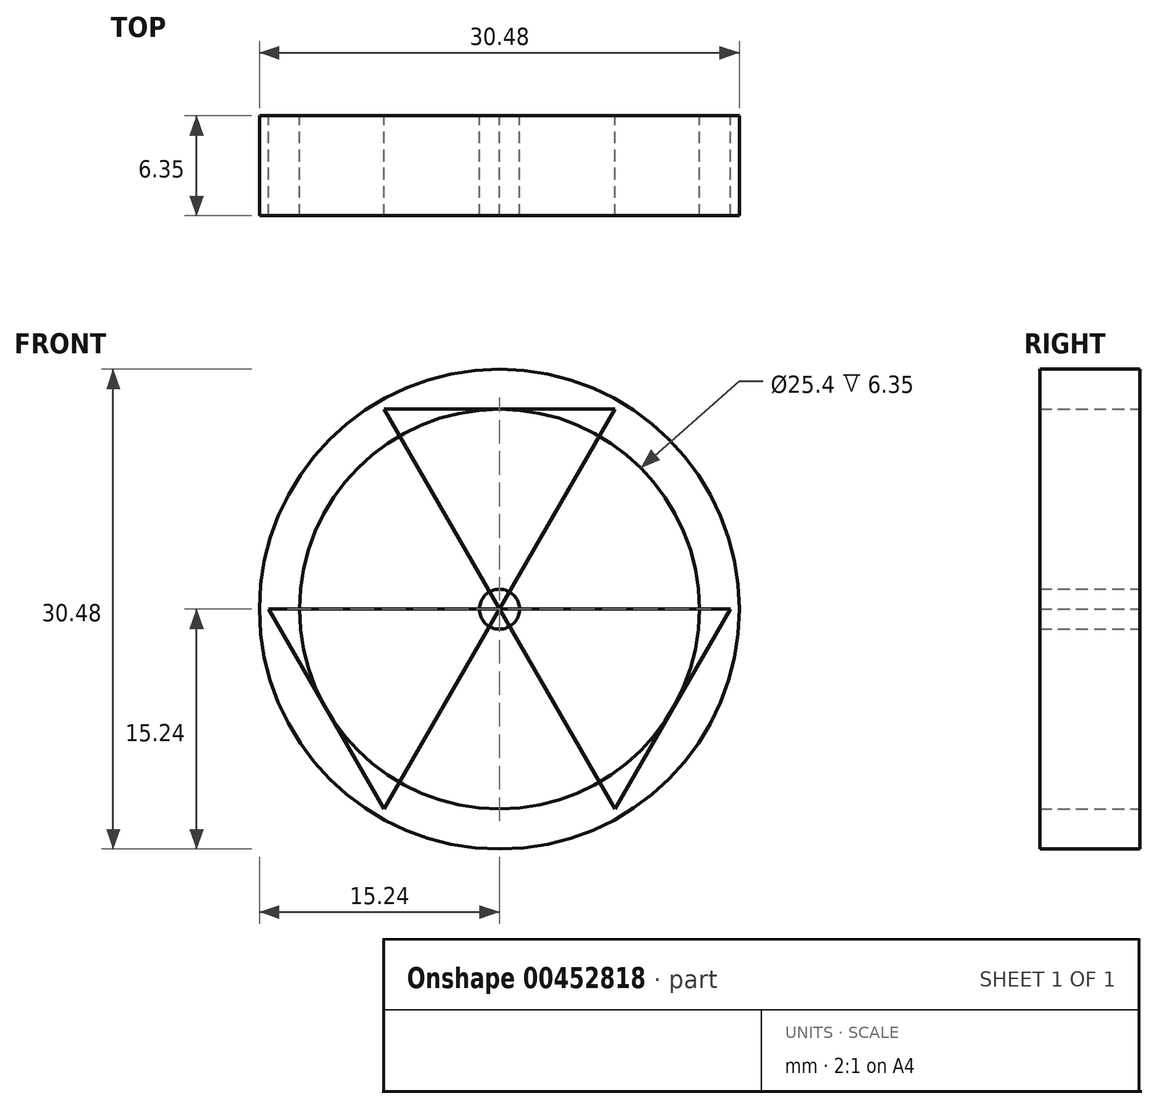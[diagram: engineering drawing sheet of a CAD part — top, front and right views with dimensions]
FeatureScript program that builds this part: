
annotation { "Feature Type Name" : "Feature", "Feature Type Description" : "" }
export const myFeature = defineFeature(function(context is Context, id is Id, definition is map)
    precondition{}
    {
        {
            var Q0;
            Q0=qCreatedBy(makeId("Front.planeOp"),FACE);
            var sketch = newSketch(context, id + "F0", { "sketchPlane" : qUnion([Q0])});
            skCircle(sketch, "E0.cCircle", {"center": v(0, 0) * mm, "radius": 12.7 * mm, "construction": true});
            skLineSegment(sketch, "E0.0", {"start": v(-7.33, 12.7) * mm, "end": v(7.33, 12.7) * mm});
            skLineSegment(sketch, "E0.1", {"start": v(7.33, 12.7) * mm, "end": v(14.66, 0) * mm});
            skLineSegment(sketch, "E0.2", {"start": v(14.66, 0) * mm, "end": v(7.33, -12.7) * mm});
            skLineSegment(sketch, "E0.3", {"start": v(7.33, -12.7) * mm, "end": v(-7.33, -12.7) * mm});
            skLineSegment(sketch, "E0.4", {"start": v(-7.33, -12.7) * mm, "end": v(-14.66, 0) * mm});
            skLineSegment(sketch, "E0.5", {"start": v(-14.66, 0) * mm, "end": v(-7.33, 12.7) * mm});
            skPoint(sketch, "E0.0.midPoint", {"position": v(0, 12.7) * mm});
            skLineSegment(sketch, "E1", {"start": v(-7.33, 12.7) * mm, "end": v(0, 0) * mm});
            skLineSegment(sketch, "E2", {"start": v(7.33, 12.7) * mm, "end": v(0, 0) * mm});
            skLineSegment(sketch, "E3", {"start": v(-14.66, 0) * mm, "end": v(0, 0) * mm});
            skLineSegment(sketch, "E4", {"start": v(-7.33, -12.7) * mm, "end": v(0, 0) * mm});
            skLineSegment(sketch, "E5", {"start": v(7.33, -12.7) * mm, "end": v(0, 0) * mm});
            skLineSegment(sketch, "E6", {"start": v(14.66, 0) * mm, "end": v(0, 0) * mm});
            skSolve(sketch);
        }
        {
            var Q0;
            Q0=makeQuery(id+"F0.imprint","IMPRINT",FACE,{"disambiguationData":[TD([[makeQuery(id+"F0.imprint","IMPRINT",EDGE,{"derivedFrom":sQuery(id+"F0.wireOp",EDGE,"E0.0")}),-1.0]])]});
            var Q1;
            Q1=makeQuery(id+"F0.imprint","IMPRINT",FACE,{"disambiguationData":[TD([[makeQuery(id+"F0.imprint","IMPRINT",EDGE,{"derivedFrom":sQuery(id+"F0.wireOp",EDGE,"E0.4")}),-1.0]])]});
            var Q2;
            Q2=makeQuery(id+"F0.imprint","IMPRINT",FACE,{"disambiguationData":[TD([[makeQuery(id+"F0.imprint","IMPRINT",EDGE,{"derivedFrom":sQuery(id+"F0.wireOp",EDGE,"E0.2")}),-1.0]])]});
            extrude(context, id + "F1", {"entities" : qUnion([Q0, Q1, Q2]), "depth" : 6.35 * mm});
        }
        {
            var Q0;
            Q0=qCreatedBy(makeId("Front.planeOp"),FACE);
            var sketch = newSketch(context, id + "F2", { "sketchPlane" : qUnion([Q0])});
            skCircle(sketch, "E7", {"center": v(0, 0) * mm, "radius": 12.7 * mm});
            skCircle(sketch, "E8", {"center": v(0, 0) * mm, "radius": 15.24 * mm});
            skSolve(sketch);
        }
        {
            var Q0;
            Q0=makeQuery(id+"F2.imprint","IMPRINT",FACE,{"disambiguationData":[TD([[makeQuery(id+"F2.imprint","IMPRINT",EDGE,{"derivedFrom":sQuery(id+"F2.wireOp",EDGE,"E7")}),-1.0]])]});
            extrude(context, id + "F3", {"entities" : qUnion([Q0]), "depth" : 6.35 * mm});
        }
        {
            var Q0;
            Q0=qCreatedBy(makeId("Front.planeOp"),FACE);
            var sketch = newSketch(context, id + "F4", { "sketchPlane" : qUnion([Q0])});
            skCircle(sketch, "E9", {"center": v(0, 0) * mm, "radius": 1.27 * mm});
            skSolve(sketch);
        }
        {
            var Q0;
            Q0=makeQuery(id+"F4.imprint","IMPRINT",FACE,{"disambiguationData":[TD([[makeQuery(id+"F4.imprint","IMPRINT",EDGE,{"derivedFrom":sQuery(id+"F4.wireOp",EDGE,"E9")}),1.0]])]});
            extrude(context, id + "F5", {"entities" : qUnion([Q0]), "depth" : 6.35 * mm});
        }
    });
